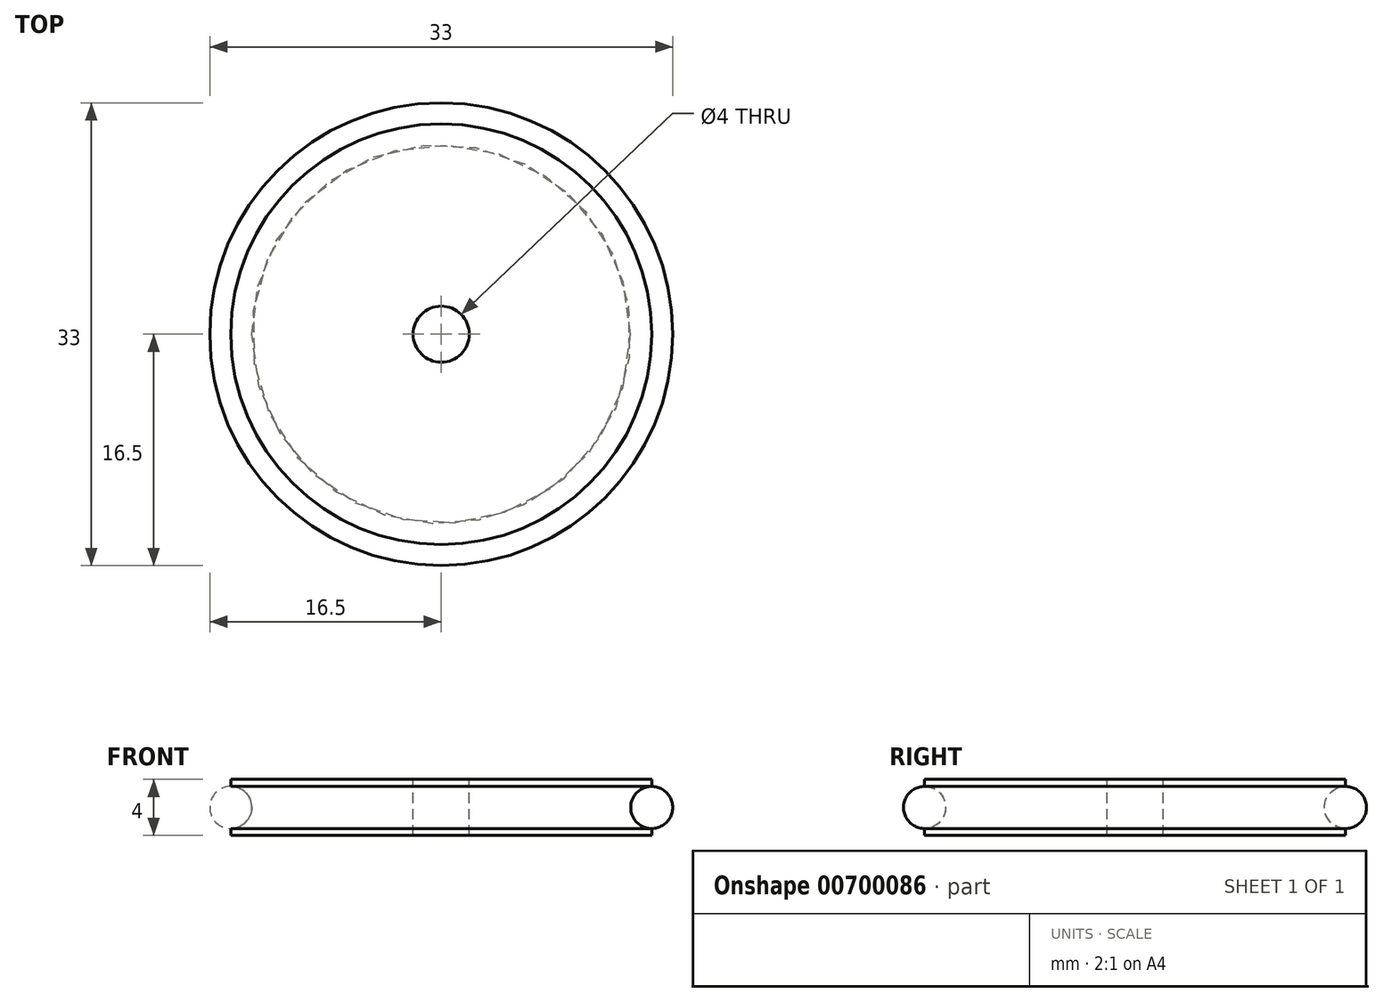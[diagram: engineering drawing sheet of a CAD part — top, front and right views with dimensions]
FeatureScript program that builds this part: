
annotation { "Feature Type Name" : "Feature", "Feature Type Description" : "" }
export const myFeature = defineFeature(function(context is Context, id is Id, definition is map)
    precondition{}
    {
        {
            var Q0;
            Q0=qCreatedBy(makeId("Top.planeOp"),FACE);
            var sketch = newSketch(context, id + "F0", { "sketchPlane" : qUnion([Q0])});
            skCircle(sketch, "E0", {"center": v(0, 0) * mm, "radius": 15 * mm});
            skSolve(sketch);
        }
        {
            var Q0;
            Q0 = qSketchRegion(id + "F0", true);
            extrude(context, id + "F1", {"entities" : qUnion([Q0]), "depth" : 4 * mm, "offsetDistance" : 25 * mm});
        }
        {
            var Q0;
            Q0=qCreatedBy(makeId("Right.planeOp"),FACE);
            var sketch = newSketch(context, id + "F2", { "sketchPlane" : qUnion([Q0])});
            skLineSegment(sketch, "E1", {"start": v(0, 0) * mm, "end": v(-15, 0) * mm, "construction": true});
            skLineSegment(sketch, "E2", {"start": v(-15, 0) * mm, "end": v(-15, 2) * mm, "construction": true});
            skCircle(sketch, "E3", {"center": v(-15, 2) * mm, "radius": 1.5 * mm});
            skLineSegment(sketch, "E4", {"start": v(0, 0) * mm, "end": v(0, 12.62) * mm});
            skSolve(sketch);
        }
        {
            var Q0;
            Q0=makeQuery(id+"F2.imprint","IMPRINT",FACE,{"disambiguationData":[TD([[makeQuery(id+"F2.imprint","IMPRINT",EDGE,{"derivedFrom":sQuery(id+"F2.wireOp",EDGE,"E3")}),1.0]])]});
            var Q1;
            Q1=sQuery(id+"F2.wireOp",EDGE,"E3");
            var Q2;
            Q2=sQuery(id+"F2.wireOp",EDGE,"E4");
            revolve(context, id + "F3", {"operationType" : NewBodyOperationType.REMOVE, "entities" : qUnion([Q0]), "surfaceEntities" : qUnion([Q1]), "axis" : qUnion([Q2]), "revolveType" : RevolveType.FULL, "oppositeDirection" : true});
        }
        {
            var Q0;
            Q0=makeQuery(id+"F1.opExtrude","CAP_FACE",FACE,{"disambiguationData":[OSD([sQuery(id+"F0.wireOp",EDGE,"E0")])],"isStart":false});
            var sketch = newSketch(context, id + "F4", { "sketchPlane" : qUnion([Q0])});
            skCircle(sketch, "E5", {"center": v(0, 0) * mm, "radius": 2 * mm});
            skSolve(sketch);
        }
        {
            var Q0;
            Q0=sQuery(id+"F4.wireOp",VERTEX,"E5.center");
            var Q1;
            Q1=makeQuery(id+"F1.opExtrude","SWEPT_BODY",BODY,{"disambiguationData":[OSD([sQuery(id+"F0.wireOp",EDGE,"E0")])]});
            hole(context, id + "F5", {"style" : HoleStyle.SIMPLE, "endStyle" : HoleEndStyle.THROUGH, "holeDiameter" : 4 * mm, "majorDiameter" : 5 * mm, "isTappedThrough" : true, "tappedDepth" : 12 * mm, "tapClearance" : 3, "locations" : qUnion([Q0]), "scope" : qUnion([Q1])});
        }
        {
            var Q0;
            Q0=makeQuery(id+"F2.imprint","IMPRINT",FACE,{"disambiguationData":[TD([[makeQuery(id+"F2.imprint","IMPRINT",EDGE,{"derivedFrom":sQuery(id+"F2.wireOp",EDGE,"E3")}),1.0]])]});
            var Q1;
            Q1=sQuery(id+"F2.wireOp",EDGE,"E4");
            revolve(context, id + "F6", {"entities" : qUnion([Q0]), "axis" : qUnion([Q1]), "revolveType" : RevolveType.FULL});
        }
    });
